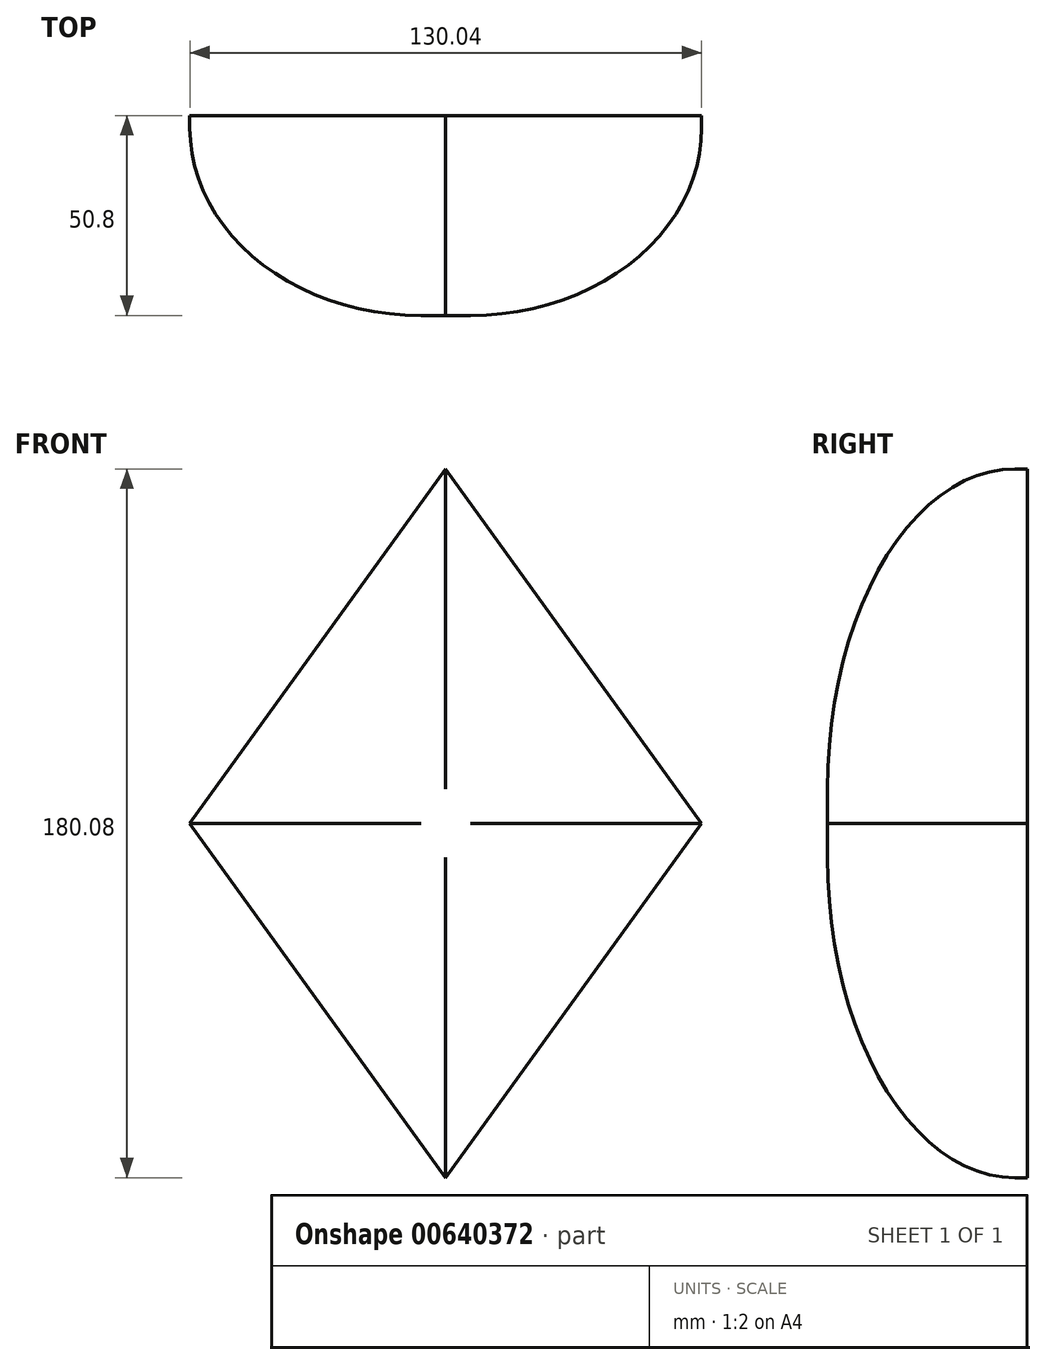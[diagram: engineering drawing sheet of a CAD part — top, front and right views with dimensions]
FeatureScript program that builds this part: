
annotation { "Feature Type Name" : "Feature", "Feature Type Description" : "" }
export const myFeature = defineFeature(function(context is Context, id is Id, definition is map)
    precondition{}
    {
        {
            var Q0;
            Q0=qCreatedBy(makeId("Front.planeOp"),FACE);
            var sketch = newSketch(context, id + "F0", { "sketchPlane" : qUnion([Q0])});
            skLineSegment(sketch, "E0", {"start": v(0, 90.04) * mm, "end": v(-65.02, 0) * mm});
            skLineSegment(sketch, "E1", {"start": v(-65.02, 0) * mm, "end": v(0, -90.04) * mm});
            skLineSegment(sketch, "E2", {"start": v(0, -90.04) * mm, "end": v(65.02, 0) * mm});
            skLineSegment(sketch, "E3", {"start": v(65.02, 0) * mm, "end": v(0, 90.04) * mm});
            skSolve(sketch);
        }
        {
            var Q0;
            Q0 = qSketchRegion(id + "F0", true);
            extrude(context, id + "F1", {"entities" : qUnion([Q0]), "depth" : 50.8 * mm, "offsetDistance" : 25.4 * mm});
        }
        {
            var Q0;
            Q0=makeQuery(id+"F1.opExtrude","CAP_FACE",FACE,{"disambiguationData":[OSD([sQuery(id+"F0.wireOp",EDGE,"E0"),sQuery(id+"F0.wireOp",EDGE,"E1"),sQuery(id+"F0.wireOp",EDGE,"E2"),sQuery(id+"F0.wireOp",EDGE,"E3")])],"isStart":false});
            fillet(context, id + "F2", {"entities" : qUnion([Q0]), "radius" : 47.62 * mm, "tangentPropagation" : true, "allowEdgeOverflow" : false});
        }
    });
